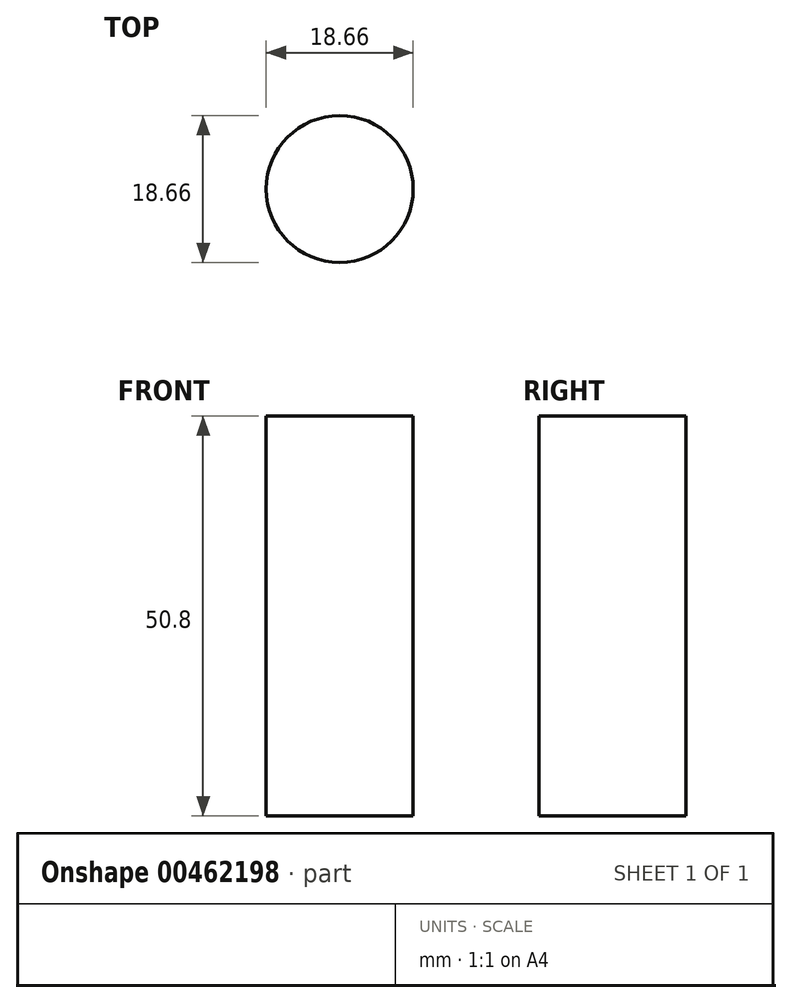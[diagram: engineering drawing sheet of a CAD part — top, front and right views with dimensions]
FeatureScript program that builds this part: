
annotation { "Feature Type Name" : "Feature", "Feature Type Description" : "" }
export const myFeature = defineFeature(function(context is Context, id is Id, definition is map)
    precondition{}
    {
        {
            var Q0;
            Q0=qCreatedBy(makeId("Top.planeOp"),FACE);
            var sketch = newSketch(context, id + "F0", { "sketchPlane" : qUnion([Q0])});
            skCircle(sketch, "E0", {"center": v(0, 0) * mm, "radius": 9.33 * mm});
            skSolve(sketch);
        }
        {
            var Q0;
            Q0 = qSketchRegion(id + "F0", true);
            extrude(context, id + "F1", {"entities" : qUnion([Q0]), "depth" : 50.8 * mm, "offsetDistance" : 25.4 * mm});
        }
    });
